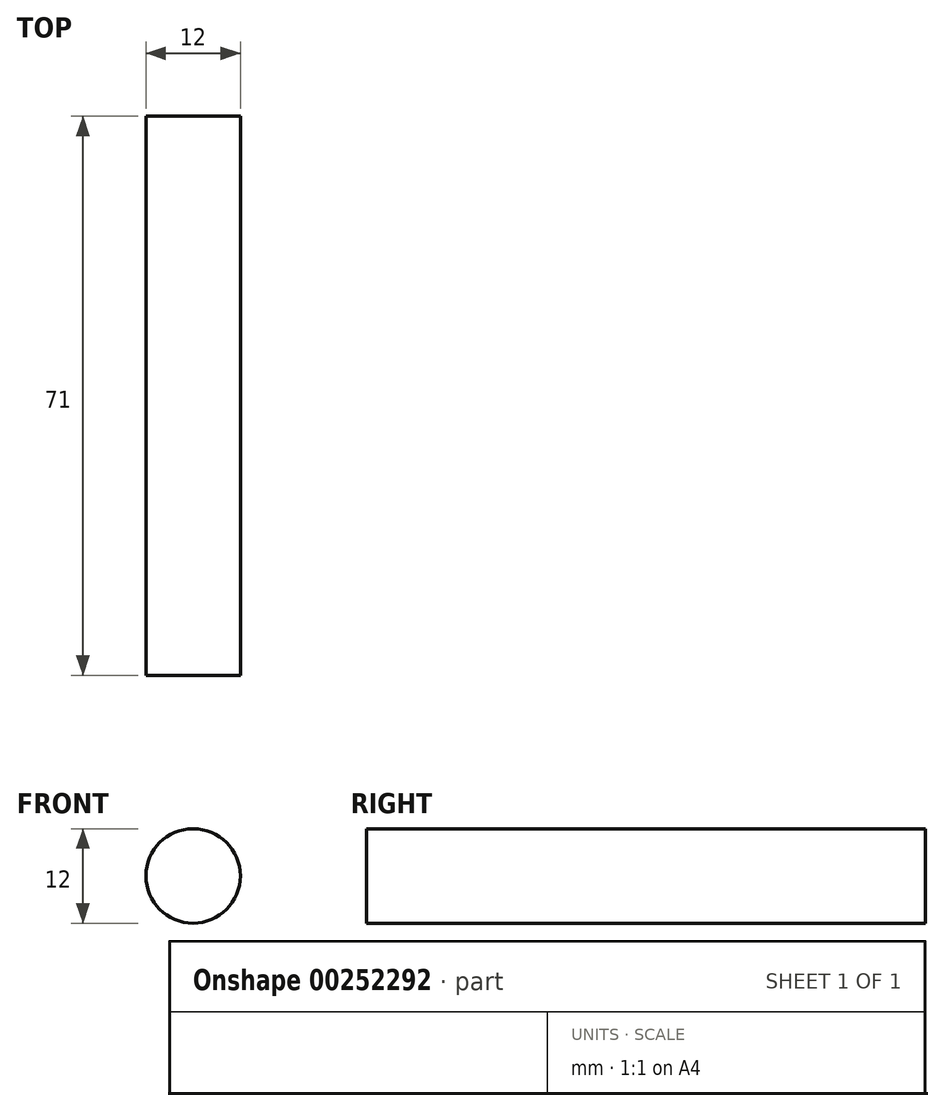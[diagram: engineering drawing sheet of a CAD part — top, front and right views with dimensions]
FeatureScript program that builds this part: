
annotation { "Feature Type Name" : "Feature", "Feature Type Description" : "" }
export const myFeature = defineFeature(function(context is Context, id is Id, definition is map)
    precondition{}
    {
        {
            var Q0;
            Q0=qCreatedBy(makeId("Front.planeOp"),FACE);
            var sketch = newSketch(context, id + "F0", { "sketchPlane" : qUnion([Q0])});
            skCircle(sketch, "E0", {"center": v(0, 0) * mm, "radius": 6 * mm});
            skSolve(sketch);
        }
        {
            var Q0;
            Q0=makeQuery(id+"F0.imprint","IMPRINT",FACE,{"disambiguationData":[TD([[makeQuery(id+"F0.imprint","IMPRINT",EDGE,{"derivedFrom":sQuery(id+"F0.wireOp",EDGE,"E0")}),1.0]])]});
            extrude(context, id + "F1", {"entities" : qUnion([Q0]), "depth" : 71 * mm});
        }
    });
